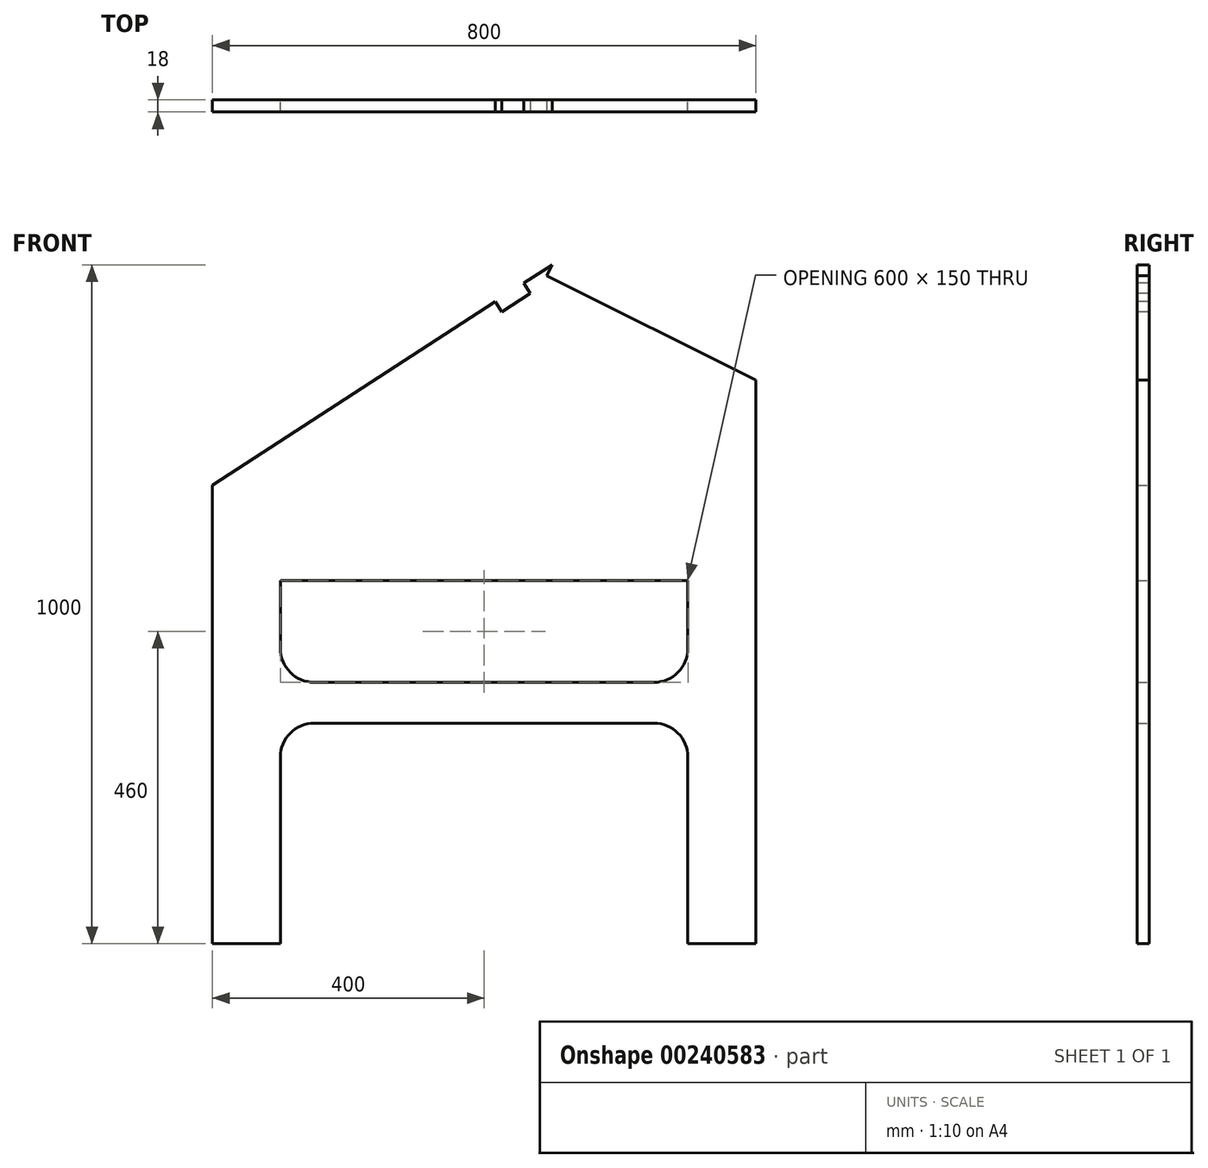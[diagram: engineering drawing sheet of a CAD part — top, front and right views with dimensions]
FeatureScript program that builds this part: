
annotation { "Feature Type Name" : "Feature", "Feature Type Description" : "" }
export const myFeature = defineFeature(function(context is Context, id is Id, definition is map)
    precondition{}
    {
        {
            var Q0;
            Q0=qCreatedBy(makeId("Front.planeOp"),FACE);
            var sketch = newSketch(context, id + "F0", { "sketchPlane" : qUnion([Q0])});
            skLineSegment(sketch, "E0.bottom", {"start": v(0, 0) * mm, "end": v(800, 0) * mm});
            skLineSegment(sketch, "E0.top", {"start": v(0, 1000) * mm, "end": v(800, 1000) * mm});
            skLineSegment(sketch, "E0.left", {"start": v(0, 0) * mm, "end": v(0, 1000) * mm});
            skLineSegment(sketch, "E0.right", {"start": v(800, 0) * mm, "end": v(800, 1000) * mm});
            skLineSegment(sketch, "E1.bottom", {"start": v(100, 0) * mm, "end": v(700, 0) * mm});
            skLineSegment(sketch, "E1.top", {"start": v(150, 325) * mm, "end": v(650, 325) * mm});
            skLineSegment(sketch, "E1.left", {"start": v(100, 0) * mm, "end": v(100, 275) * mm});
            skLineSegment(sketch, "E1.right", {"start": v(700, 0) * mm, "end": v(700, 275) * mm});
            skLineSegment(sketch, "E2", {"start": v(0, 675) * mm, "end": v(500, 1000) * mm});
            skLineSegment(sketch, "E3", {"start": v(500, 1000) * mm, "end": v(800, 850) * mm});
            skLineSegment(sketch, "E4.bottom", {"start": v(150, 385) * mm, "end": v(650, 385) * mm});
            skLineSegment(sketch, "E4.top", {"start": v(100, 535) * mm, "end": v(700, 535) * mm});
            skLineSegment(sketch, "E4.left", {"start": v(100, 435) * mm, "end": v(100, 535) * mm});
            skLineSegment(sketch, "E4.right", {"start": v(700, 435) * mm, "end": v(700, 535) * mm});
            skPoint(sketch, "E5.visualSharp", {"position": v(100, 325) * mm});
            skArc(sketch, "E5.filletArc", {"start": v(150, 325) * mm, "mid": v(114.64, 310.36) * mm, "end": v(100, 275) * mm});
            skPoint(sketch, "E6.visualSharp", {"position": v(700, 325) * mm});
            skArc(sketch, "E6.filletArc", {"start": v(700, 275) * mm, "mid": v(685.36, 310.36) * mm, "end": v(650, 325) * mm});
            skPoint(sketch, "E7.visualSharp", {"position": v(100, 385) * mm});
            skArc(sketch, "E7.filletArc", {"start": v(100, 435) * mm, "mid": v(114.64, 399.64) * mm, "end": v(150, 385) * mm});
            skPoint(sketch, "E8.visualSharp", {"position": v(700, 385) * mm});
            skArc(sketch, "E8.filletArc", {"start": v(650, 385) * mm, "mid": v(685.36, 399.64) * mm, "end": v(700, 435) * mm});
            skSolve(sketch);
        }
        {
            var Q0;
            Q0=makeQuery(id+"F0.imprint","IMPRINT",FACE,{"disambiguationData":[TD([[makeQuery(id+"F0.imprint","IMPRINT",EDGE,{"derivedFrom":sQuery(id+"F0.wireOp",EDGE,"E1.top")}),1.0]])]});
            extrude(context, id + "F1", {"entities" : qUnion([Q0]), "depth" : 18 * mm});
        }
        {
            var Q0;
            Q0=makeQuery(id+"F1.opExtrude","CAP_FACE",FACE,{"disambiguationData":[OSD([sQuery(id+"F0.wireOp",EDGE,"E0.bottom"),sQuery(id+"F0.wireOp",EDGE,"E0.left"),sQuery(id+"F0.wireOp",EDGE,"E0.right"),sQuery(id+"F0.wireOp",EDGE,"E1.top"),sQuery(id+"F0.wireOp",EDGE,"E1.left"),sQuery(id+"F0.wireOp",EDGE,"E1.right"),sQuery(id+"F0.wireOp",EDGE,"E2"),sQuery(id+"F0.wireOp",EDGE,"E3"),sQuery(id+"F0.wireOp",EDGE,"E4.bottom"),sQuery(id+"F0.wireOp",EDGE,"E4.top"),sQuery(id+"F0.wireOp",EDGE,"E4.left"),sQuery(id+"F0.wireOp",EDGE,"E4.right"),sQuery(id+"F0.wireOp",EDGE,"E5.filletArc"),sQuery(id+"F0.wireOp",EDGE,"E6.filletArc"),sQuery(id+"F0.wireOp",EDGE,"E7.filletArc"),sQuery(id+"F0.wireOp",EDGE,"E8.filletArc")])],"isStart":false});
            var sketch = newSketch(context, id + "F2", { "sketchPlane" : qUnion([Q0])});
            skLineSegment(sketch, "E9", {"start": v(125.77, 756.75) * mm, "end": v(119.23, 766.8) * mm, "construction": true});
            skLineSegment(sketch, "E10", {"start": v(119.23, 766.8) * mm, "end": v(161.15, 794.06) * mm, "construction": true});
            skLineSegment(sketch, "E11", {"start": v(161.15, 794.06) * mm, "end": v(167.69, 784) * mm, "construction": true});
            skLineSegment(sketch, "E12", {"start": v(167.69, 784) * mm, "end": v(125.77, 756.75) * mm, "construction": true});
            skLineSegment(sketch, "E13", {"start": v(332.31, 891) * mm, "end": v(325.77, 901.06) * mm, "construction": true});
            skLineSegment(sketch, "E14", {"start": v(325.77, 901.06) * mm, "end": v(367.7, 928.31) * mm, "construction": true});
            skLineSegment(sketch, "E15", {"start": v(367.7, 928.31) * mm, "end": v(374.23, 918.25) * mm, "construction": true});
            skLineSegment(sketch, "E16", {"start": v(374.23, 918.25) * mm, "end": v(332.31, 891) * mm, "construction": true});
            skSolve(sketch);
        }
        {
            var Q0;
            Q0=makeQuery(id+"FIqgvMlhu0AXTPI_1.boolean.opBoolean","MERGE",FACE,{"derivedFrom":[makeQuery(id+"F1.opExtrude","CAP_FACE",FACE,{"disambiguationData":[OSD([sQuery(id+"F0.wireOp",EDGE,"E0.bottom"),sQuery(id+"F0.wireOp",EDGE,"E0.left"),sQuery(id+"F0.wireOp",EDGE,"E0.right"),sQuery(id+"F0.wireOp",EDGE,"E1.top"),sQuery(id+"F0.wireOp",EDGE,"E1.left"),sQuery(id+"F0.wireOp",EDGE,"E1.right"),sQuery(id+"F0.wireOp",EDGE,"E2"),sQuery(id+"F0.wireOp",EDGE,"E3"),sQuery(id+"F0.wireOp",EDGE,"E4.bottom"),sQuery(id+"F0.wireOp",EDGE,"E4.top"),sQuery(id+"F0.wireOp",EDGE,"E4.left"),sQuery(id+"F0.wireOp",EDGE,"E4.right"),sQuery(id+"F0.wireOp",EDGE,"E5.filletArc"),sQuery(id+"F0.wireOp",EDGE,"E6.filletArc"),sQuery(id+"F0.wireOp",EDGE,"E7.filletArc"),sQuery(id+"F0.wireOp",EDGE,"E8.filletArc")])],"isStart":false}),makeQuery(id+"FIqgvMlhu0AXTPI_1.opExtrude","CAP_FACE",FACE,{"disambiguationData":[OSD([sQuery(id+"F2.wireOp",EDGE,"E9"),sQuery(id+"F2.wireOp",EDGE,"E10"),sQuery(id+"F2.wireOp",EDGE,"E11"),sQuery(id+"F2.wireOp",EDGE,"E12")])],"isStart":true}),makeQuery(id+"FIqgvMlhu0AXTPI_1.opExtrude","CAP_FACE",FACE,{"disambiguationData":[OSD([sQuery(id+"F2.wireOp",EDGE,"E13"),sQuery(id+"F2.wireOp",EDGE,"E14"),sQuery(id+"F2.wireOp",EDGE,"E15"),sQuery(id+"F2.wireOp",EDGE,"E16")])],"isStart":true})]});
            var sketch = newSketch(context, id + "F3", { "sketchPlane" : qUnion([Q0])});
            skLineSegment(sketch, "E17", {"start": v(607.33, 946.33) * mm, "end": v(612.7, 957.07) * mm, "construction": true});
            skLineSegment(sketch, "E18", {"start": v(567.98, 979.43) * mm, "end": v(612.7, 957.07) * mm, "construction": true});
            skLineSegment(sketch, "E19", {"start": v(567.98, 979.43) * mm, "end": v(562.6, 968.7) * mm, "construction": true});
            skLineSegment(sketch, "E20", {"start": v(607.33, 946.33) * mm, "end": v(562.6, 968.7) * mm, "construction": true});
            skLineSegment(sketch, "E21", {"start": v(692.67, 903.67) * mm, "end": v(698.04, 914.4) * mm, "construction": true});
            skLineSegment(sketch, "E22", {"start": v(698.04, 914.4) * mm, "end": v(742.76, 892.04) * mm, "construction": true});
            skLineSegment(sketch, "E23", {"start": v(742.76, 892.04) * mm, "end": v(737.4, 881.3) * mm, "construction": true});
            skLineSegment(sketch, "E24", {"start": v(737.4, 881.3) * mm, "end": v(692.67, 903.67) * mm, "construction": true});
            skSolve(sketch);
        }
        {
            var Q0;
            Q0=makeQuery(id+"FIqgvMlhu0AXTPI_1.boolean.opBoolean","MERGE",FACE,{"derivedFrom":[makeQuery(id+"F1.opExtrude","CAP_FACE",FACE,{"disambiguationData":[OSD([sQuery(id+"F0.wireOp",EDGE,"E0.bottom"),sQuery(id+"F0.wireOp",EDGE,"E0.left"),sQuery(id+"F0.wireOp",EDGE,"E0.right"),sQuery(id+"F0.wireOp",EDGE,"E1.top"),sQuery(id+"F0.wireOp",EDGE,"E1.left"),sQuery(id+"F0.wireOp",EDGE,"E1.right"),sQuery(id+"F0.wireOp",EDGE,"E2"),sQuery(id+"F0.wireOp",EDGE,"E3"),sQuery(id+"F0.wireOp",EDGE,"E4.bottom"),sQuery(id+"F0.wireOp",EDGE,"E4.top"),sQuery(id+"F0.wireOp",EDGE,"E4.left"),sQuery(id+"F0.wireOp",EDGE,"E4.right"),sQuery(id+"F0.wireOp",EDGE,"E5.filletArc"),sQuery(id+"F0.wireOp",EDGE,"E6.filletArc"),sQuery(id+"F0.wireOp",EDGE,"E7.filletArc"),sQuery(id+"F0.wireOp",EDGE,"E8.filletArc")])],"isStart":false}),makeQuery(id+"FIqgvMlhu0AXTPI_1.opExtrude","CAP_FACE",FACE,{"disambiguationData":[OSD([sQuery(id+"F2.wireOp",EDGE,"E9"),sQuery(id+"F2.wireOp",EDGE,"E10"),sQuery(id+"F2.wireOp",EDGE,"E11"),sQuery(id+"F2.wireOp",EDGE,"E12")])],"isStart":true}),makeQuery(id+"FIqgvMlhu0AXTPI_1.opExtrude","CAP_FACE",FACE,{"disambiguationData":[OSD([sQuery(id+"F2.wireOp",EDGE,"E13"),sQuery(id+"F2.wireOp",EDGE,"E14"),sQuery(id+"F2.wireOp",EDGE,"E15"),sQuery(id+"F2.wireOp",EDGE,"E16")])],"isStart":true}),makeQuery(id+"FIqgvMlhu0AXTPI_1.opExtrude","CAP_FACE",FACE,{"disambiguationData":[OSD([sQuery(id+"F3.wireOp",EDGE,"E17"),sQuery(id+"F3.wireOp",EDGE,"E18"),sQuery(id+"F3.wireOp",EDGE,"E19"),sQuery(id+"F3.wireOp",EDGE,"E20")])],"isStart":true}),makeQuery(id+"FIqgvMlhu0AXTPI_1.opExtrude","CAP_FACE",FACE,{"disambiguationData":[OSD([sQuery(id+"F3.wireOp",EDGE,"E21"),sQuery(id+"F3.wireOp",EDGE,"E22"),sQuery(id+"F3.wireOp",EDGE,"E23"),sQuery(id+"F3.wireOp",EDGE,"E24")])],"isStart":true})]});
            var sketch = newSketch(context, id + "F4", { "sketchPlane" : qUnion([Q0])});
            skLineSegment(sketch, "E25", {"start": v(416.16, 945.5) * mm, "end": v(425.97, 930.4) * mm});
            skLineSegment(sketch, "E26", {"start": v(425.97, 930.4) * mm, "end": v(467.89, 957.66) * mm});
            skLineSegment(sketch, "E27", {"start": v(467.89, 957.66) * mm, "end": v(458.08, 972.75) * mm});
            skLineSegment(sketch, "E28", {"start": v(458.08, 972.75) * mm, "end": v(416.16, 945.5) * mm});
            skSolve(sketch);
        }
        {
            var Q0;
            Q0 = qSketchRegion(id + "F4", true);
            extrude(context, id + "F5", {"entities" : qUnion([Q0]), "operationType" : NewBodyOperationType.REMOVE, "endBound" : BoundingType.UP_TO_NEXT, "oppositeDirection" : true, "depth" : 25 * mm});
        }
        {
            var Q0;
            {var subQ2=sQuery(id+"F0.wireOp",EDGE,"E0.left");Q0=makeQuery(id+"F2.imprint","IMPRINT",FACE,{"disambiguationData":[TD([[makeQuery(id+"F2.imprint","IMPRINT",EDGE,{"derivedFrom":makeQuery(id+"F1.opExtrude","CAP_EDGE",EDGE,{"disambiguationData":[OSD([subQ2])],"isStart":false})}),-1.0]])]});}
            var sketch = newSketch(context, id + "F6", { "sketchPlane" : qUnion([Q0])});
            skLineSegment(sketch, "E29", {"start": v(500, 1000) * mm, "end": v(491.95, 983.9) * mm});
            skLineSegment(sketch, "E30", {"start": v(491.95, 983.9) * mm, "end": v(849.72, 805.01) * mm});
            skLineSegment(sketch, "E31", {"start": v(849.72, 805.01) * mm, "end": v(857.77, 821.11) * mm});
            skLineSegment(sketch, "E32", {"start": v(857.77, 821.11) * mm, "end": v(500, 1000) * mm});
            skSolve(sketch);
        }
        {
            var Q0;
            Q0 = qSketchRegion(id + "F6", true);
            extrude(context, id + "F7", {"entities" : qUnion([Q0]), "operationType" : NewBodyOperationType.REMOVE, "endBound" : BoundingType.UP_TO_NEXT, "oppositeDirection" : true, "depth" : 25 * mm, "offsetDistance" : 25 * mm});
        }
    });
